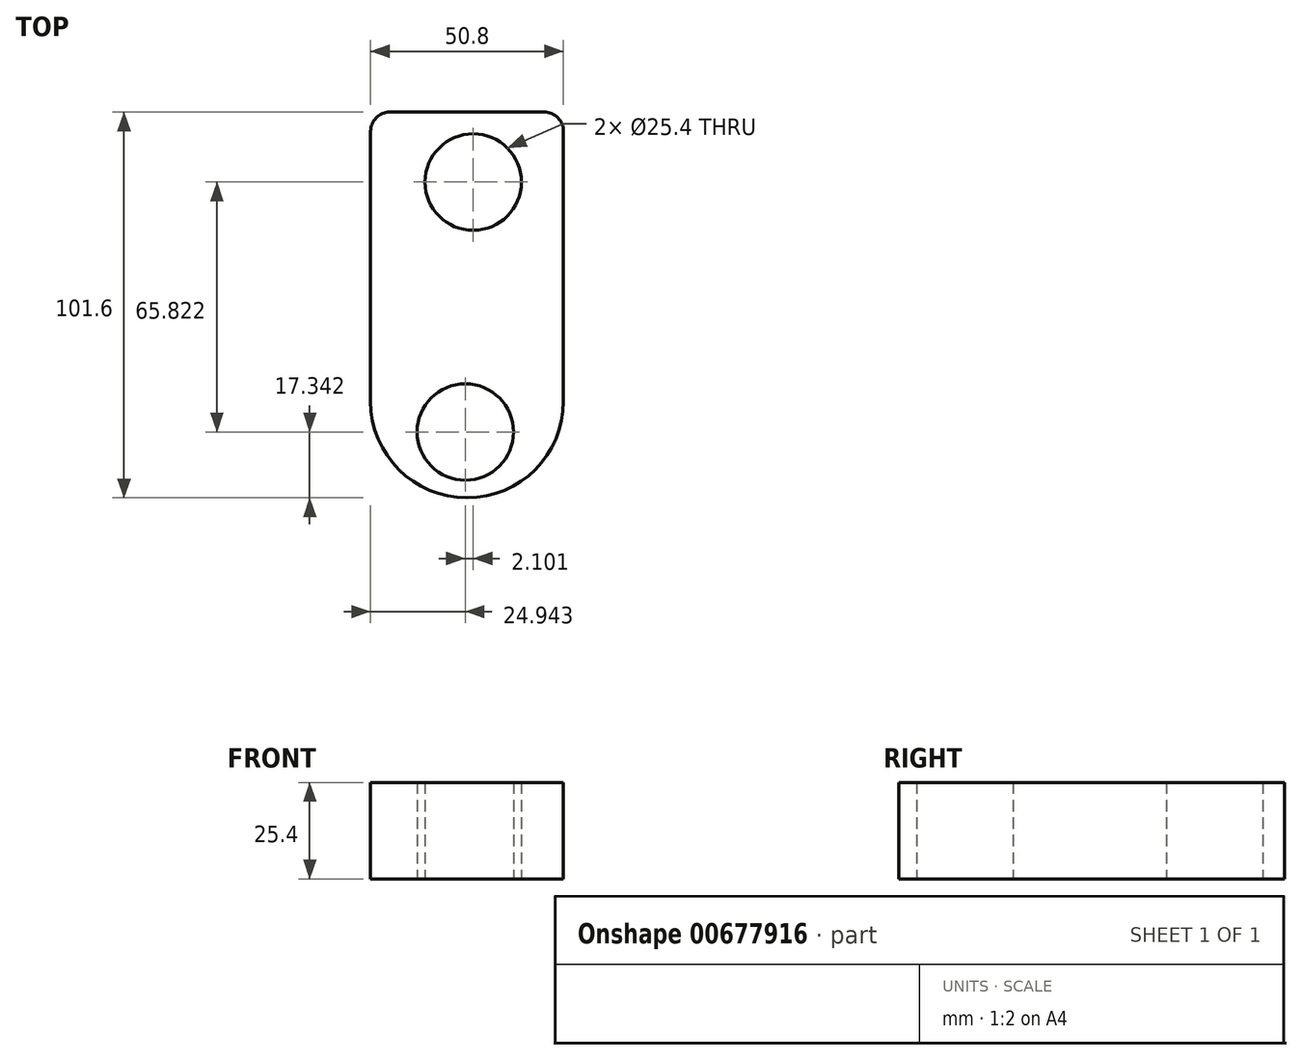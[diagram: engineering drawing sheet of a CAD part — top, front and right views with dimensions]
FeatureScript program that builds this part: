
annotation { "Feature Type Name" : "Feature", "Feature Type Description" : "" }
export const myFeature = defineFeature(function(context is Context, id is Id, definition is map)
    precondition{}
    {
        {
            var Q0;
            Q0=qCreatedBy(makeId("Top.planeOp"),FACE);
            var sketch = newSketch(context, id + "F0", { "sketchPlane" : qUnion([Q0])});
            skLineSegment(sketch, "E0", {"start": v(-20.2, 48.65) * mm, "end": v(-20.2, -52.95) * mm});
            skLineSegment(sketch, "E1", {"start": v(-20.2, -52.95) * mm, "end": v(30.6, -52.95) * mm});
            skLineSegment(sketch, "E2", {"start": v(30.6, -52.95) * mm, "end": v(30.6, 48.65) * mm});
            skLineSegment(sketch, "E3", {"start": v(30.6, 48.65) * mm, "end": v(-20.2, 48.65) * mm});
            skSolve(sketch);
        }
        {
            var Q0;
            Q0 = qSketchRegion(id + "F0", true);
            extrude(context, id + "F1", {"entities" : qUnion([Q0]), "depth" : 25.4 * mm, "offsetDistance" : 25.4 * mm});
        }
        {
            var Q0;
            Q0=qCreatedBy(makeId("Top.planeOp"),FACE);
            var sketch = newSketch(context, id + "F2", { "sketchPlane" : qUnion([Q0])});
            skPoint(sketch, "E4", {"position": v(4.73, -35.6) * mm});
            skCircle(sketch, "E5", {"center": v(4.73, -35.6) * mm, "radius": 12.7 * mm});
            skSolve(sketch);
        }
        {
            var Q0;
            Q0 = qSketchRegion(id + "F2", true);
            extrude(context, id + "F3", {"entities" : qUnion([Q0]), "operationType" : NewBodyOperationType.REMOVE, "endBound" : BoundingType.THROUGH_ALL, "oppositeDirection" : true, "depth" : 25.4 * mm, "offsetDistance" : 25.4 * mm});
        }
        {
            var Q0;
            Q0=sQuery(id+"F2.wireOp",VERTEX,"E4");
            var Q1;
            Q1=makeQuery(id+"F1.opExtrude","SWEPT_BODY",BODY,{"disambiguationData":[OSD([sQuery(id+"F0.wireOp",EDGE,"E0"),sQuery(id+"F0.wireOp",EDGE,"E1"),sQuery(id+"F0.wireOp",EDGE,"E2"),sQuery(id+"F0.wireOp",EDGE,"E3")])]});
            hole(context, id + "F4", {"style" : HoleStyle.SIMPLE, "endStyle" : HoleEndStyle.THROUGH, "oppositeDirection" : true, "holeDiameter" : 25.4 * mm, "majorDiameter" : 6.35 * mm, "isTappedThrough" : true, "tappedDepth" : 12.7 * mm, "tapClearance" : 3, "locations" : qUnion([Q0]), "scope" : qUnion([Q1])});
        }
        {
            var Q0;
            Q0=makeQuery(id+"F0.imprint","IMPRINT",FACE,{"disambiguationData":[TD([[makeQuery(id+"F0.imprint","IMPRINT",EDGE,{"derivedFrom":sQuery(id+"F0.wireOp",EDGE,"E0")}),1.0]])]});
            var sketch = newSketch(context, id + "F5", { "sketchPlane" : qUnion([Q0])});
            skPoint(sketch, "E6", {"position": v(6.83, 30.21) * mm});
            skSolve(sketch);
        }
        {
            var Q0;
            Q0=sQuery(id+"F5.wireOp",VERTEX,"E6");
            var Q1;
            Q1=makeQuery(id+"F1.opExtrude","SWEPT_BODY",BODY,{"disambiguationData":[OSD([sQuery(id+"F0.wireOp",EDGE,"E0"),sQuery(id+"F0.wireOp",EDGE,"E1"),sQuery(id+"F0.wireOp",EDGE,"E2"),sQuery(id+"F0.wireOp",EDGE,"E3")])]});
            hole(context, id + "F6", {"style" : HoleStyle.SIMPLE, "endStyle" : HoleEndStyle.THROUGH, "oppositeDirection" : true, "holeDiameter" : 25.4 * mm, "majorDiameter" : 6.35 * mm, "isTappedThrough" : true, "tappedDepth" : 12.7 * mm, "tapClearance" : 3, "locations" : qUnion([Q0]), "scope" : qUnion([Q1])});
        }
        {
            var Q0;
            Q0=makeQuery(id+"F1.opExtrude","SWEPT_EDGE",EDGE,{"disambiguationData":[OSD([sQuery(id+"F0.wireOp",EDGE,"E0"),sQuery(id+"F0.wireOp",EDGE,"E1")])]});
            var Q1;
            Q1=makeQuery(id+"F1.opExtrude","SWEPT_EDGE",EDGE,{"disambiguationData":[OSD([sQuery(id+"F0.wireOp",EDGE,"E1"),sQuery(id+"F0.wireOp",EDGE,"E2")])]});
            fillet(context, id + "F7", {"entities" : qUnion([Q0, Q1]), "radius" : 25.4 * mm, "tangentPropagation" : true, "allowEdgeOverflow" : false});
        }
        {
            var Q0;
            Q0=makeQuery(id+"F1.opExtrude","SWEPT_EDGE",EDGE,{"disambiguationData":[OSD([sQuery(id+"F0.wireOp",EDGE,"E0"),sQuery(id+"F0.wireOp",EDGE,"E3")])]});
            var Q1;
            Q1=makeQuery(id+"F1.opExtrude","SWEPT_EDGE",EDGE,{"disambiguationData":[OSD([sQuery(id+"F0.wireOp",EDGE,"E2"),sQuery(id+"F0.wireOp",EDGE,"E3")])]});
            fillet(context, id + "F8", {"entities" : qUnion([Q0, Q1]), "radius" : 5.08 * mm, "tangentPropagation" : true, "allowEdgeOverflow" : false});
        }
    });
